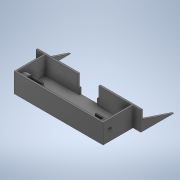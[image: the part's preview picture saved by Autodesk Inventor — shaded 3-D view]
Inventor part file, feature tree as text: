
AUTODESK INVENTOR PART (.ipt)
format: ipt  version: 2020 (Build 240168000, 168)  size: 290,816 bytes
history: native  units: in
note: dims shown in document units (in); Inventor stores cm internally (conversion verified against a paired STEP export)
features: sketch x8, extrude x7, mirror x2, projected_geometry x2
ambient origin geometry x8: Origin, YZ Plane, XZ Plane, XY Plane, X Axis, Y Axis, Z Axis, Center Point
bodies: Solid1 (feature_tree)
feature tree (19):
  extrude  "Extrusion1"  Depth=2.3622in
  extrude  "Extrusion2"  Depth=1.3386in TaperAngle=0.0deg
  extrude  "Extrusion5"  Depth=0.7874in
  extrude  "Extrusion6"  Depth=0.7874in
  extrude  "Extrusion7"  Depth=0.4429in TaperAngle=0.0deg
  mirror  "Mirror2"
  extrude  "Extrusion9"  Depth=0.7874in
  extrude  "Extrusion11"  Depth=0.7874in TaperAngle=0.0deg
  mirror  "Mirror4"
  sketch  "Sketch14"  dims[d32=0.5906in d33=0.1181in d36=6.4567in d37=2.126in d40=0.7874in d41=0.5118in d42=3.2283in d43=1.3386in d44=0.3937in d45=0.0in d53=0.1181in d54=0.0in d55=0.6102in d60=2.3622in d61=0.7874in d62=0.3937in d63=0.4724in d64=0.2362in d50=0.0197in d51=0.0344in d52=0.0197in]
  sketch  "Sketch1"  dims[d0=6.6929in d1=2.3622in]
  sketch  "Sketch2"  dims[d2=0.1181in d3=0.0in d5=1.3386in d6=0.0in]
  projected_geometry  "Projected Loop1"
  sketch  "Sketch4"  dims[d13=0.7874in d14=0.7874in]
  sketch  "Sketch7"  dims[d17=0.6299in d18=0.7874in]
  sketch  "Sketch8"  dims[d20=0.0787in d21=0.4429in d22=0.0in]
  projected_geometry  "Projected Loop5"
  sketch  "Sketch9"  dims[d25=0.7874in d26=0.0in d27=0.2362in]
  sketch  "Sketch13"  dims[d28=0.7874in d30=0.4626in d31=0.0in]
